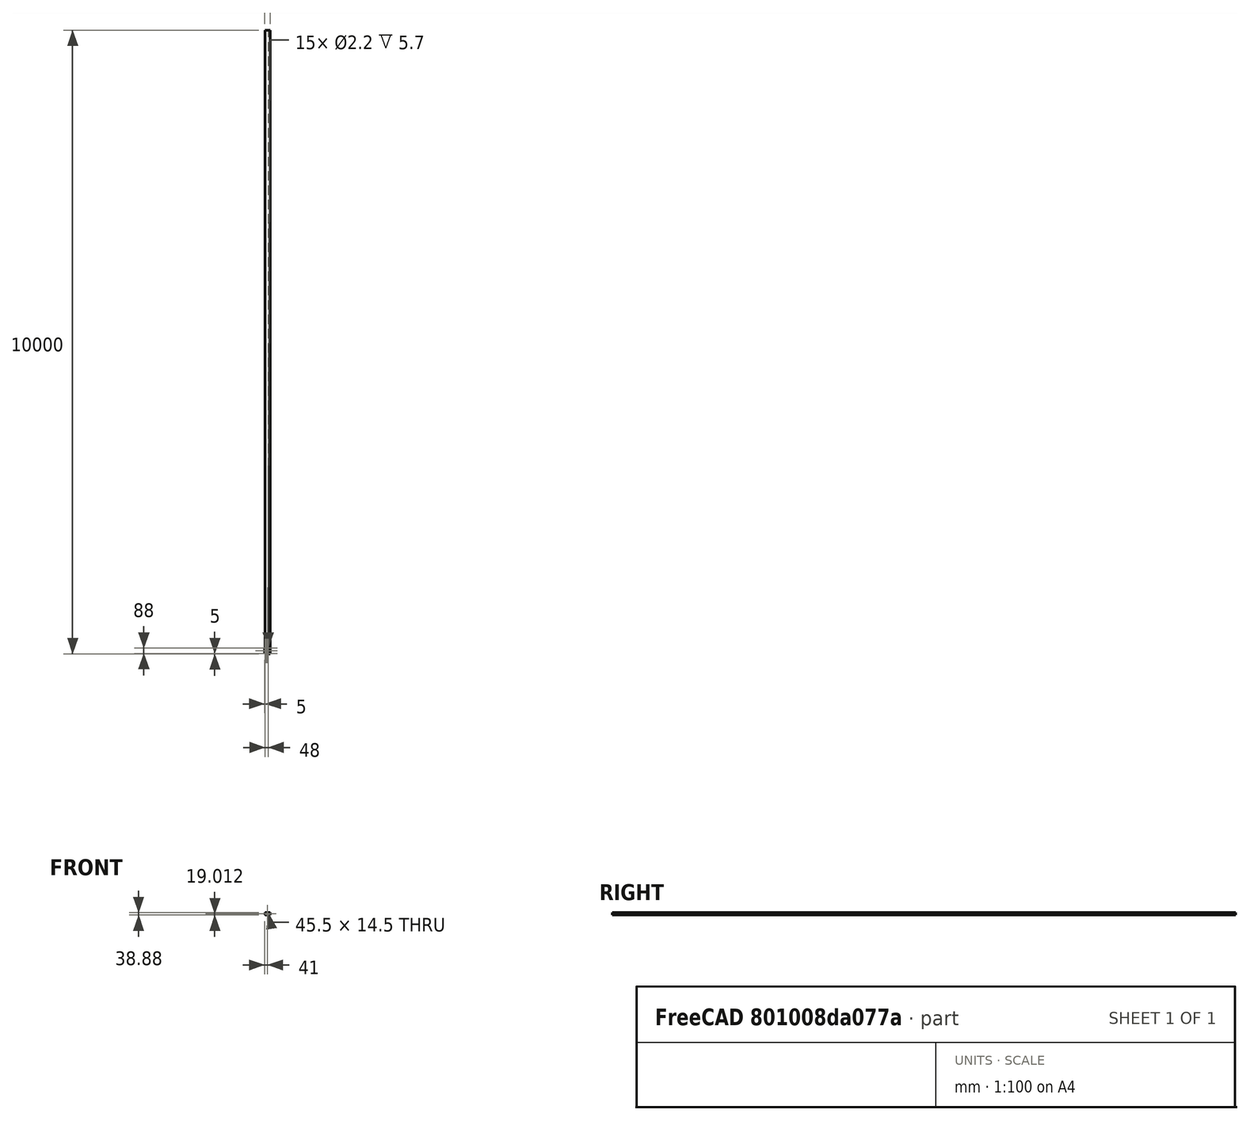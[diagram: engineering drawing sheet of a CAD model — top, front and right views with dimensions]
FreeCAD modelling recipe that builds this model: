
FCSTD DOCUMENT  (FreeCAD 0.15R4671 (Git))
Label: 8mm-strip_feeder_x4
License: CreativeCommons Attribution-ShareAlike
LicenseURL: http://creativecommons.org/licenses/by-sa/4.0/
objects: Part::Box×27, Part::Prism×25, Sketcher::SketchObject×3, PartDesign::Pocket×3, Part::Feature×1, Part::MultiFuse×1, Part::Cut×1, PartDesign::LinearPattern×1, PartDesign::Chamfer×1, PartDesign::Fillet×1, Mesh::Feature×1
note: 67 computed .brp shape members not serialized (recipe doc carries the construction recipe); baked Part::Feature solids carry a one-line shape summary decoded from their .brp

FEATURE [Part::Feature] Part__Mirroring  label="Fillet print"
  Placement = pos=(-12,99,-1) rot=(1,0,0;1.5708rad)
  shape: bbox 58 x 98 x 10 mm, 92 faces (baked)
FEATURE [Part::Box] cube103
  Height = 0.8
  Length = 8
  Width = 100
FEATURE [Part::Prism] prism099
  Circumradius = 0.835
  Height = 3
  Placement = pos=(2,0,-1) rot=(0,0,1;0rad)
  Polygon = 20
FEATURE [Part::Box] cube104
  Height = 2
  Length = 2
  Placement = pos=(3.5,1,0.2) rot=(0,0,1;0rad)
  Width = 1.5
FEATURE [Part::Prism] prism100
  Circumradius = 0.835
  Height = 3
  Placement = pos=(2,4,-1) rot=(0,0,1;0rad)
  Polygon = 20
FEATURE [Part::Box] cube105
  Height = 2
  Length = 2
  Placement = pos=(3.5,5,0.2) rot=(0,0,1;0rad)
  Width = 1.5
FEATURE [Part::Prism] prism101
  Circumradius = 0.835
  Height = 3
  Placement = pos=(2,8,-1) rot=(0,0,1;0rad)
  Polygon = 20
FEATURE [Part::Box] cube106
  Height = 2
  Length = 2
  Placement = pos=(3.5,9,0.2) rot=(0,0,1;0rad)
  Width = 1.5
FEATURE [Part::Prism] prism102
  Circumradius = 0.835
  Height = 3
  Placement = pos=(2,12,-1) rot=(0,0,1;0rad)
  Polygon = 20
FEATURE [Part::Box] cube107
  Height = 2
  Length = 2
  Placement = pos=(3.5,13,0.2) rot=(0,0,1;0rad)
  Width = 1.5
FEATURE [Part::Prism] prism103
  Circumradius = 0.835
  Height = 3
  Placement = pos=(2,16,-1) rot=(0,0,1;0rad)
  Polygon = 20
FEATURE [Part::Box] cube108
  Height = 2
  Length = 2
  Placement = pos=(3.5,17,0.2) rot=(0,0,1;0rad)
  Width = 1.5
FEATURE [Part::Prism] prism104
  Circumradius = 0.835
  Height = 3
  Placement = pos=(2,20,-1) rot=(0,0,1;0rad)
  Polygon = 20
FEATURE [Part::Box] cube109
  Height = 2
  Length = 2
  Placement = pos=(3.5,21,0.2) rot=(0,0,1;0rad)
  Width = 1.5
FEATURE [Part::Prism] prism105
  Circumradius = 0.835
  Height = 3
  Placement = pos=(2,24,-1) rot=(0,0,1;0rad)
  Polygon = 20
FEATURE [Part::Box] cube110
  Height = 2
  Length = 2
  Placement = pos=(3.5,25,0.2) rot=(0,0,1;0rad)
  Width = 1.5
FEATURE [Part::Prism] prism106
  Circumradius = 0.835
  Height = 3
  Placement = pos=(2,28,-1) rot=(0,0,1;0rad)
  Polygon = 20
FEATURE [Part::Box] cube111
  Height = 2
  Length = 2
  Placement = pos=(3.5,29,0.2) rot=(0,0,1;0rad)
  Width = 1.5
FEATURE [Part::Prism] prism107
  Circumradius = 0.835
  Height = 3
  Placement = pos=(2,32,-1) rot=(0,0,1;0rad)
  Polygon = 20
FEATURE [Part::Box] cube112
  Height = 2
  Length = 2
  Placement = pos=(3.5,33,0.2) rot=(0,0,1;0rad)
  Width = 1.5
FEATURE [Part::Prism] prism108
  Circumradius = 0.835
  Height = 3
  Placement = pos=(2,36,-1) rot=(0,0,1;0rad)
  Polygon = 20
FEATURE [Part::Box] cube113
  Height = 2
  Length = 2
  Placement = pos=(3.5,37,0.2) rot=(0,0,1;0rad)
  Width = 1.5
FEATURE [Part::Prism] prism109
  Circumradius = 0.835
  Height = 3
  Placement = pos=(2,40,-1) rot=(0,0,1;0rad)
  Polygon = 20
FEATURE [Part::Box] cube114
  Height = 2
  Length = 2
  Placement = pos=(3.5,41,0.2) rot=(0,0,1;0rad)
  Width = 1.5
FEATURE [Part::Prism] prism110
  Circumradius = 0.835
  Height = 3
  Placement = pos=(2,44,-1) rot=(0,0,1;0rad)
  Polygon = 20
FEATURE [Part::Box] cube115
  Height = 2
  Length = 2
  Placement = pos=(3.5,45,0.2) rot=(0,0,1;0rad)
  Width = 1.5
FEATURE [Part::Prism] prism111
  Circumradius = 0.835
  Height = 3
  Placement = pos=(2,48,-1) rot=(0,0,1;0rad)
  Polygon = 20
FEATURE [Part::Box] cube116
  Height = 2
  Length = 2
  Placement = pos=(3.5,49,0.2) rot=(0,0,1;0rad)
  Width = 1.5
FEATURE [Part::Prism] prism112
  Circumradius = 0.835
  Height = 3
  Placement = pos=(2,52,-1) rot=(0,0,1;0rad)
  Polygon = 20
FEATURE [Part::Box] cube117
  Height = 2
  Length = 2
  Placement = pos=(3.5,53,0.2) rot=(0,0,1;0rad)
  Width = 1.5
FEATURE [Part::Prism] prism113
  Circumradius = 0.835
  Height = 3
  Placement = pos=(2,56,-1) rot=(0,0,1;0rad)
  Polygon = 20
FEATURE [Part::Box] cube118
  Height = 2
  Length = 2
  Placement = pos=(3.5,57,0.2) rot=(0,0,1;0rad)
  Width = 1.5
FEATURE [Part::Prism] prism114
  Circumradius = 0.835
  Height = 3
  Placement = pos=(2,60,-1) rot=(0,0,1;0rad)
  Polygon = 20
FEATURE [Part::Box] cube119
  Height = 2
  Length = 2
  Placement = pos=(3.5,61,0.2) rot=(0,0,1;0rad)
  Width = 1.5
FEATURE [Part::Prism] prism115
  Circumradius = 0.835
  Height = 3
  Placement = pos=(2,64,-1) rot=(0,0,1;0rad)
  Polygon = 20
FEATURE [Part::Box] cube120
  Height = 2
  Length = 2
  Placement = pos=(3.5,65,0.2) rot=(0,0,1;0rad)
  Width = 1.5
FEATURE [Part::Prism] prism116
  Circumradius = 0.835
  Height = 3
  Placement = pos=(2,68,-1) rot=(0,0,1;0rad)
  Polygon = 20
FEATURE [Part::Box] cube121
  Height = 2
  Length = 2
  Placement = pos=(3.5,69,0.2) rot=(0,0,1;0rad)
  Width = 1.5
FEATURE [Part::Prism] prism117
  Circumradius = 0.835
  Height = 3
  Placement = pos=(2,72,-1) rot=(0,0,1;0rad)
  Polygon = 20
FEATURE [Part::Box] cube122
  Height = 2
  Length = 2
  Placement = pos=(3.5,73,0.2) rot=(0,0,1;0rad)
  Width = 1.5
FEATURE [Part::Prism] prism118
  Circumradius = 0.835
  Height = 3
  Placement = pos=(2,76,-1) rot=(0,0,1;0rad)
  Polygon = 20
FEATURE [Part::Box] cube123
  Height = 2
  Length = 2
  Placement = pos=(3.5,77,0.2) rot=(0,0,1;0rad)
  Width = 1.5
FEATURE [Part::Prism] prism119
  Circumradius = 0.835
  Height = 3
  Placement = pos=(2,80,-1) rot=(0,0,1;0rad)
  Polygon = 20
FEATURE [Part::Box] cube124
  Height = 2
  Length = 2
  Placement = pos=(3.5,81,0.2) rot=(0,0,1;0rad)
  Width = 1.5
FEATURE [Part::Prism] prism120
  Circumradius = 0.835
  Height = 3
  Placement = pos=(2,84,-1) rot=(0,0,1;0rad)
  Polygon = 20
FEATURE [Part::Box] cube125
  Height = 2
  Length = 2
  Placement = pos=(3.5,85,0.2) rot=(0,0,1;0rad)
  Width = 1.5
FEATURE [Part::Prism] prism121
  Circumradius = 0.835
  Height = 3
  Placement = pos=(2,88,-1) rot=(0,0,1;0rad)
  Polygon = 20
FEATURE [Part::Box] cube126
  Height = 2
  Length = 2
  Placement = pos=(3.5,89,0.2) rot=(0,0,1;0rad)
  Width = 1.5
FEATURE [Part::Prism] prism122
  Circumradius = 0.835
  Height = 3
  Placement = pos=(2,92,-1) rot=(0,0,1;0rad)
  Polygon = 20
FEATURE [Part::Box] cube127
  Height = 2
  Length = 2
  Placement = pos=(3.5,93,0.2) rot=(0,0,1;0rad)
  Width = 1.5
FEATURE [Part::Prism] prism123
  Circumradius = 0.835
  Height = 3
  Placement = pos=(2,96,-1) rot=(0,0,1;0rad)
  Polygon = 20
FEATURE [Part::Box] cube128
  Height = 2
  Length = 2
  Placement = pos=(3.5,97,0.2) rot=(0,0,1;0rad)
  Width = 1.5
FEATURE [Part::MultiFuse] Group003
  Shapes = -> [prism099,cube104,prism100,cube105,prism101,cube106,prism102,cube107,prism103,cube108,prism104,cube109,prism105,cube110,prism106,cube111,prism107,cube112,prism108,cube113,prism109,cube114,prism110,cube115,prism111,cube116,prism112,cube117,prism113,cube118,prism114,cube119,prism115,cube120,prism116,cube121,prism117,cube122,prism118,cube123,prism119,cube124,prism120,cube125,prism121,cube126,prism122,+3 more]
FEATURE [Part::Cut] difference003
  Base = -> cube103
  Placement = pos=(4.5,0,10) rot=(0,0,1;0rad)
  Tool = -> Group003
FEATURE [Part::Box] Box  label="Cube"
  Height = 11.6
  Length = 70
  Placement = pos=(-7.5,0,0) rot=(0,0,1;0rad)
  Width = 200
FEATURE [Sketcher::SketchObject] Sketch002  label="base"
  Placement = pos=(-7.5,0,0) rot=(1,0,0;1.5708rad)
  Support = -> Box [Face3]
  sketch-geometry (17):
    g0: LineSegment [constr] StartX=0 StartY=11.6 StartZ=0 EndX=0 EndY=0 EndZ=0
    g1: LineSegment [constr] StartX=0 StartY=0 StartZ=0 EndX=12 EndY=0 EndZ=0
    g2: LineSegment [constr] StartX=12 StartY=11.6 StartZ=0 EndX=9.75 EndY=11.6 EndZ=0
    g3: LineSegment StartX=10.05 StartY=10 StartZ=0 EndX=7.25 EndY=10 EndZ=0
    g4: LineSegment [constr] StartX=2.25 StartY=11.6 StartZ=0 EndX=0 EndY=11.6 EndZ=0
    g5: LineSegment [constr] StartX=12 StartY=11.6 StartZ=0 EndX=12 EndY=0 EndZ=0
    g6: LineSegment [constr] StartX=0 StartY=0 StartZ=0 EndX=1.95 EndY=10 EndZ=0
    g7: LineSegment [constr] StartX=12 StartY=0 StartZ=0 EndX=10.05 EndY=10 EndZ=0
    g8: LineSegment StartX=1.95 StartY=10 StartZ=0 EndX=1.95 EndY=10.4 EndZ=0
    g9: LineSegment StartX=1.95 StartY=10.4 StartZ=0 EndX=2.25 EndY=11.6 EndZ=0
    g10: LineSegment StartX=9.75 StartY=11.6 StartZ=0 EndX=10.05 EndY=10.4 EndZ=0
    g11: LineSegment StartX=10.05 StartY=10.4 StartZ=0 EndX=10.05 EndY=10 EndZ=0
    g12: LineSegment StartX=7.25 StartY=10 StartZ=0 EndX=7.25 EndY=3 EndZ=0
    g13: LineSegment StartX=7.25 StartY=3 StartZ=0 EndX=2.75 EndY=3 EndZ=0
    g14: LineSegment StartX=2.75 StartY=3 StartZ=0 EndX=2.75 EndY=10 EndZ=0
    g15: LineSegment StartX=2.75 StartY=10 StartZ=0 EndX=1.95 EndY=10 EndZ=0
    g16: LineSegment StartX=2.25 StartY=11.6 StartZ=0 EndX=9.75 EndY=11.6 EndZ=0
  constraints (47):
    c: Vertical(g0)
    c: Coincident(g0,g1)
    c: Horizontal(g1)
    c: Horizontal(g2)
    c: Horizontal(g3)
    c: Horizontal(g4)
    c: Coincident(g0,g4)
    c: Coincident(g5,g2)
    c: Coincident(g5,g1)
    c: Vertical(g5)
    c: Coincident(g6,g0)
    c: Coincident(g6,g15)
    c: Coincident(g7,g1)
    c: Equal(g7,g6)
    c: DistanceX(g4,g2) = 7.5
    c: DistanceX(g1) = 12
    c: Coincident(g15,g8)
    c: Vertical(g8)
    c: Coincident(g8,g9)
    c: Coincident(g9,g4)
    c: Coincident(g2,g10)
    c: Coincident(g10,g11)
    c: Coincident(g11,g3)
    c: Vertical(g11)
    c: Equal(g11,g8)
    c: Equal(g10,g9)
    c: DistanceY(g11) = -0.4
    c: Coincident(g7,g3)
    c: Coincident(g12,g13)
    c: Coincident(g13,g14)
    c: Horizontal(g13)
    c: Vertical(g12)
    c: Vertical(g14)
    c: Tangent(g3,g15)
    c: Coincident(g14,g15)
    c: Coincident(g12,g3)
    c: DistanceX(g6,g3) = 8.1
    c: DistanceY(g14) = 7
    c: DistanceX(g15) = -0.8
    c: Distance(g4,g15) = 1.6
    c: DistanceX(g13) = -4.5
    c: Distance(g14,g1) = 10
    c: DistanceX(g0) = 0
    c: DistanceY(g0) = 0
    c: Coincident(g4,g16)
    c: Coincident(g16,g2)
    c: DistanceX(g4) = -2.25
FEATURE [PartDesign::Pocket] Pocket
  Length = 5
  Placement = pos=(-7.5,0,0) rot=(0,0,1;0rad)
  Sketch = -> Sketch002
  Type = 1
FEATURE [PartDesign::LinearPattern] LinearPattern
  Direction = -> Sketch002 [H_Axis]
  Length = 50
  Occurrences = 6
  Originals = -> [Pocket]
  Placement = pos=(-7.5,0,0) rot=(0,0,1;0rad)
FEATURE [Sketcher::SketchObject] Sketch
  ExternalGeometry = -> [LinearPattern]
  Placement = pos=(-7.5,0,0) rot=(1,0,0;1.5708rad)
  Support = -> LinearPattern [Face2]
  sketch-geometry (8):
    g0: LineSegment StartX=7.25 StartY=13.113 StartZ=0 EndX=52.75 EndY=13.113 EndZ=0
    g1: LineSegment StartX=52.75 StartY=13.113 StartZ=0 EndX=52.75 EndY=-1.3882 EndZ=0
    g2: LineSegment StartX=52.75 StartY=-1.3882 StartZ=0 EndX=7.25 EndY=-1.3882 EndZ=0
    g3: LineSegment StartX=7.25 StartY=-1.3882 StartZ=0 EndX=7.25 EndY=13.113 EndZ=0
    g4: LineSegment StartX=-5.79076 StartY=25.732 StartZ=0 EndX=76.618 EndY=25.732 EndZ=0
    g5: LineSegment StartX=76.618 StartY=25.732 StartZ=0 EndX=76.618 EndY=-13.1532 EndZ=0
    g6: LineSegment StartX=76.618 StartY=-13.1532 StartZ=0 EndX=-5.79076 EndY=-13.1532 EndZ=0
    g7: LineSegment StartX=-5.79076 StartY=-13.1532 StartZ=0 EndX=-5.79076 EndY=25.732 EndZ=0
  constraints (18):
    c: Coincident(g0,g1)
    c: Coincident(g1,g2)
    c: Coincident(g2,g3)
    c: Coincident(g3,g0)
    c: Horizontal(g0)
    c: Horizontal(g2)
    c: Vertical(g1)
    c: Vertical(g3)
    c: Coincident(g4,g5)
    c: Coincident(g5,g6)
    c: Coincident(g6,g7)
    c: Coincident(g7,g4)
    c: Horizontal(g4)
    c: Horizontal(g6)
    c: Vertical(g5)
    c: Vertical(g7)
    c: PointOnObject(g-3,g1)
    c: PointOnObject(g-4,g3)
FEATURE [PartDesign::Pocket] Pocket001
  Length = 5
  Placement = pos=(-7.5,0,0) rot=(0,0,1;0rad)
  Sketch = -> Sketch
  Type = 1
FEATURE [Sketcher::SketchObject] Sketch003
  ExternalGeometry = -> [Pocket001]
  Placement = pos=(-7.5,0,0) rot=(1,0,0;3.14159rad)
  Support = -> Pocket001 [Face49]
  sketch-geometry (11):
    g0: Circle CenterX=15 CenterY=-10 CenterZ=0 NormalX=0 NormalY=0 NormalZ=1 Radius=1
    g1: Circle CenterX=45 CenterY=-10 CenterZ=0 NormalX=0 NormalY=0 NormalZ=1 Radius=1
    g2: LineSegment [constr] StartX=15 StartY=-10 StartZ=0 EndX=45 EndY=-10 EndZ=0
    g3: LineSegment [constr] StartX=45 StartY=-10 StartZ=0 EndX=45 EndY=-190 EndZ=0
    g4: LineSegment [constr] StartX=45 StartY=-190 StartZ=0 EndX=15 EndY=-190 EndZ=0
    g5: Circle CenterX=15 CenterY=-190 CenterZ=0 NormalX=0 NormalY=0 NormalZ=1 Radius=1
    g6: Circle CenterX=45 CenterY=-190 CenterZ=0 NormalX=0 NormalY=0 NormalZ=1 Radius=1
    g7: Circle CenterX=15 CenterY=-100 CenterZ=0 NormalX=0 NormalY=0 NormalZ=1 Radius=1
    g8: Circle CenterX=45 CenterY=-100 CenterZ=0 NormalX=0 NormalY=0 NormalZ=1 Radius=1
    g9: LineSegment [constr] StartX=15 StartY=-10 StartZ=0 EndX=15 EndY=-100 EndZ=0
    g10: LineSegment [constr] StartX=15 StartY=-100 StartZ=0 EndX=15 EndY=-190 EndZ=0
  constraints (26):
    c: Coincident(g2,g3)
    c: Coincident(g3,g4)
    c: Horizontal(g2)
    c: Horizontal(g4)
    c: Vertical(g3)
    c: Coincident(g2,g0)
    c: Coincident(g1,g2)
    c: Coincident(g5,g4)
    c: Coincident(g6,g3)
    c: Equal(g6,g5)
    c: Equal(g5,g0)
    c: Equal(g0,g1)
    c: Radius(g1) = 1
    c: PointOnObject(g8,g3)
    c: Equal(g8,g7)
    c: Equal(g7,g1)
    c: Symmetric(g-3,g-5,g7)
    c: DistanceY(g4,g7) = 90
    c: Symmetric(g-6,g-4,g8)
    c: Coincident(g9,g0)
    c: Coincident(g9,g7)
    c: Vertical(g9)
    c: Coincident(g9,g10)
    c: Coincident(g10,g4)
    c: Vertical(g10)
    c: Equal(g10,g9)
FEATURE [PartDesign::Pocket] Pocket002
  Length = 5
  Placement = pos=(-7.5,0,0) rot=(0,0,1;0rad)
  Sketch = -> Sketch003
  Type = 1
FEATURE [PartDesign::Chamfer] Chamfer
  Base = -> Pocket002 [Edge76,Edge138,Edge75,Edge139,Edge77,Edge140]
  Placement = pos=(-7.5,0,0) rot=(0,0,1;0rad)
  Size = 1
FEATURE [PartDesign::Fillet] Fillet
  Base = -> Chamfer [Edge57,Edge56,Edge55,Edge53,Edge52,Edge51,Edge47,Edge46,Edge45,Edge43,Edge42,Edge41,Edge37,Edge36,Edge35,Edge33,Edge32,Edge31,Edge27,Edge26,Edge25,Edge23,Edge22,Edge21,Edge18,Edge17,Edge16,Edge14,Edge13,Edge12,Edge110,Edge109,Edge108,Edge104,Edge105,Edge106,Edge100,Edge99,Edge98,Edge96,+20 more]
  Placement = pos=(-7.5,0,0) rot=(0,0,1;0rad)
  Radius = 0.92
FEATURE [Mesh::Feature] tape_8mm
  Placement = pos=(8.5,100,8) rot=(0,0,1;3.14159rad)
